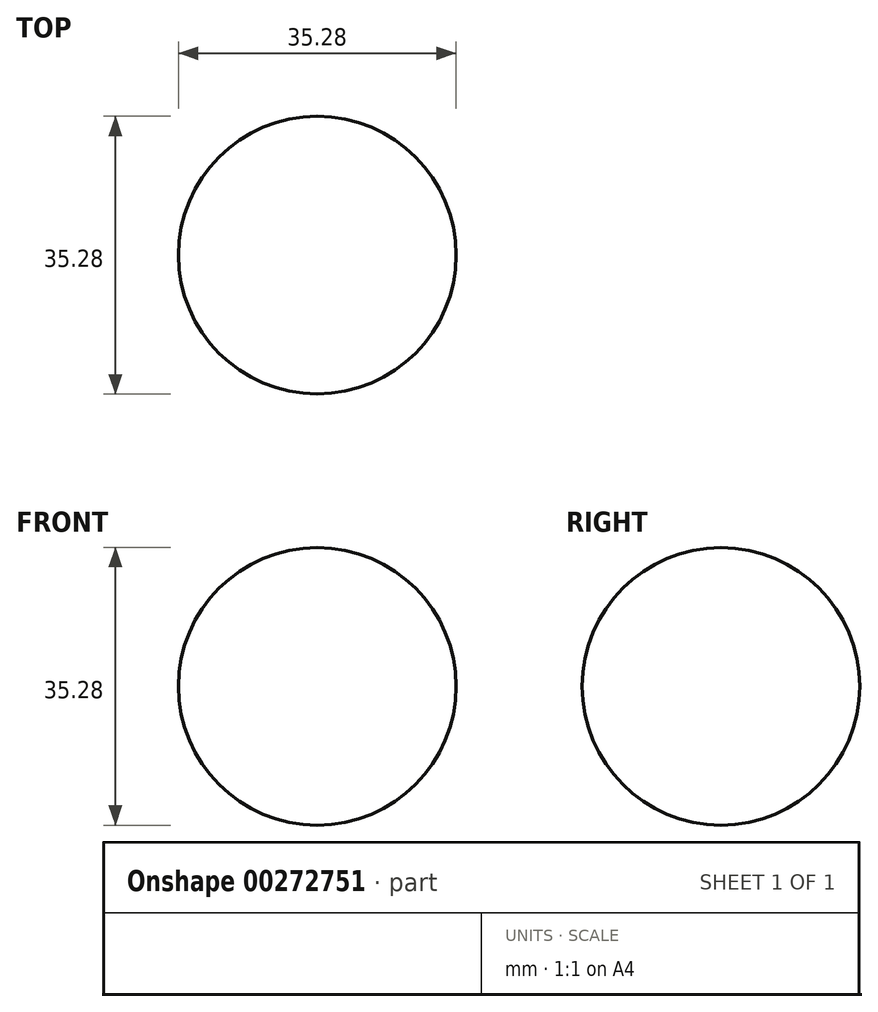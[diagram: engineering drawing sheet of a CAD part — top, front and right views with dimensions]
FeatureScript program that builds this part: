
annotation { "Feature Type Name" : "Feature", "Feature Type Description" : "" }
export const myFeature = defineFeature(function(context is Context, id is Id, definition is map)
    precondition{}
    {
        {
            var Q0;
            Q0=qCreatedBy(makeId("Front.planeOp"),FACE);
            var sketch = newSketch(context, id + "F0", { "sketchPlane" : qUnion([Q0])});
            skArc(sketch, "E0", {"start": v(0, 17.64) * mm, "mid": v(-17.64, 0) * mm, "end": v(0, -17.64) * mm});
            skLineSegment(sketch, "E1", {"start": v(0, -17.64) * mm, "end": v(0, 17.64) * mm});
            skSolve(sketch);
        }
        {
            var Q0;
            Q0 = qSketchRegion(id + "F0", true);
            var Q1;
            Q1=sQuery(id+"F0.wireOp",EDGE,"E1");
            revolve(context, id + "F1", {"entities" : qUnion([Q0]), "axis" : qUnion([Q1]), "revolveType" : RevolveType.FULL});
        }
    });
